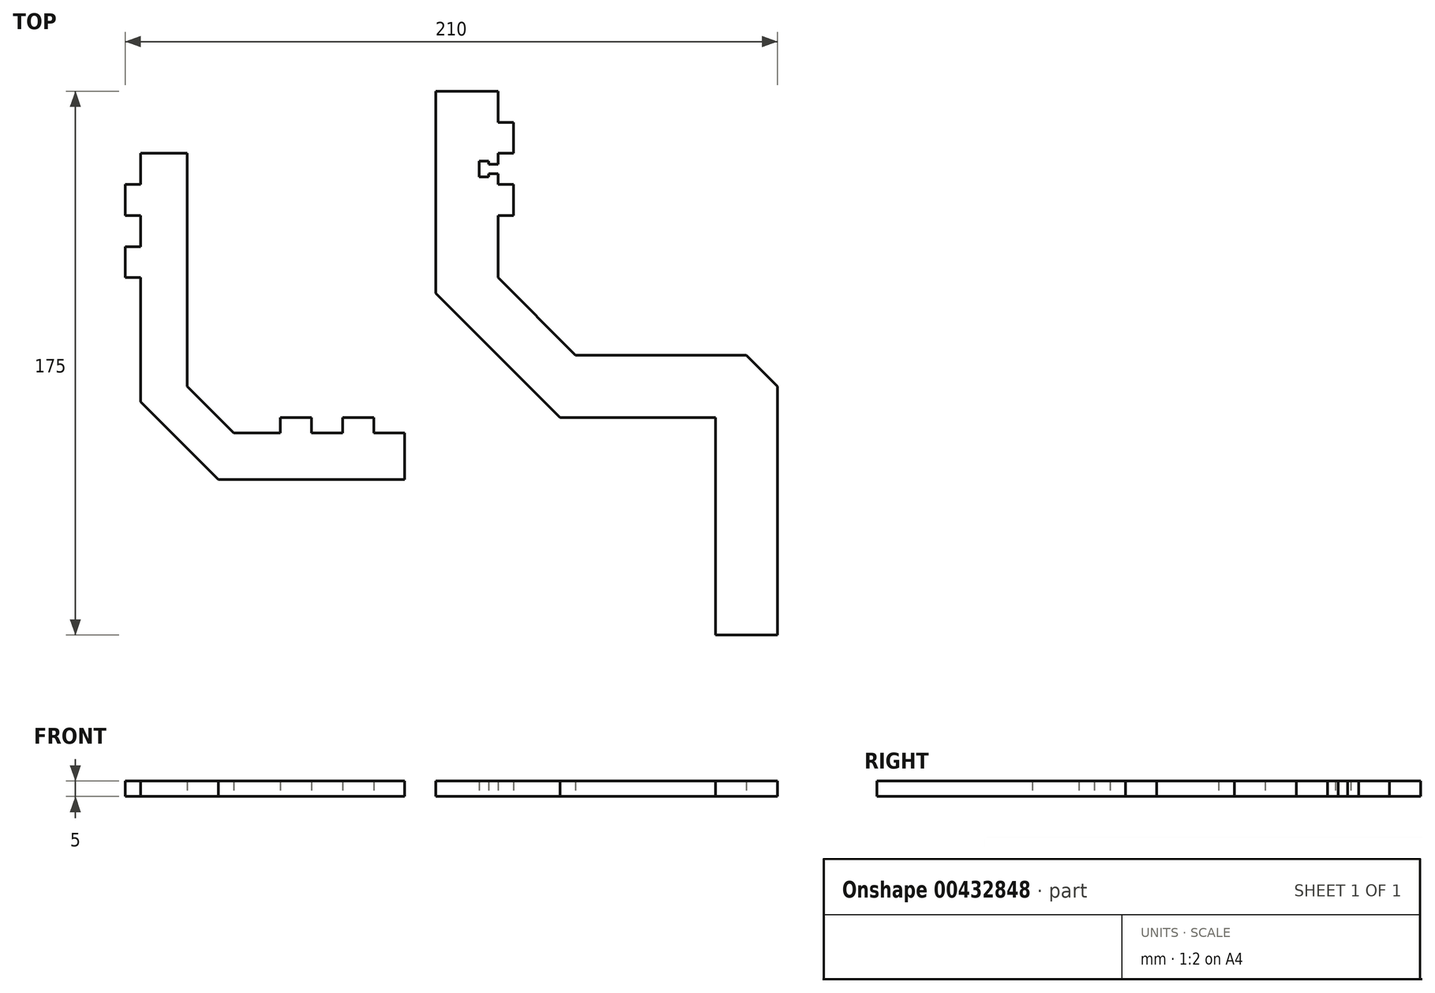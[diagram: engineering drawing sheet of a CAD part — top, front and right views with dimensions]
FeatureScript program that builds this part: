
annotation { "Feature Type Name" : "Feature", "Feature Type Description" : "" }
export const myFeature = defineFeature(function(context is Context, id is Id, definition is map)
    precondition{}
    {
        {
            var Q0;
            Q0=qCreatedBy(makeId("Top.planeOp"),FACE);
            var sketch = newSketch(context, id + "F0", { "sketchPlane" : qUnion([Q0])});
            skLineSegment(sketch, "E0.bottom", {"start": v(-20, 60) * mm, "end": v(0, 60) * mm});
            skLineSegment(sketch, "E0.left", {"start": v(-20, 60) * mm, "end": v(-20, -5) * mm});
            skLineSegment(sketch, "E0.right", {"start": v(0, 60) * mm, "end": v(0, 50) * mm});
            skLineSegment(sketch, "E1.bottom", {"start": v(25, -25) * mm, "end": v(80, -25) * mm});
            skLineSegment(sketch, "E1.top", {"start": v(20, -45) * mm, "end": v(70, -45) * mm});
            skLineSegment(sketch, "E2", {"start": v(0, 0) * mm, "end": v(25, -25) * mm});
            skLineSegment(sketch, "E3", {"start": v(-20, -5) * mm, "end": v(20, -45) * mm});
            skLineSegment(sketch, "E4.top", {"start": v(70, -115) * mm, "end": v(90, -115) * mm});
            skLineSegment(sketch, "E4.left", {"start": v(70, -45) * mm, "end": v(70, -115) * mm});
            skLineSegment(sketch, "E4.right", {"start": v(90, -35) * mm, "end": v(90, -115) * mm});
            skLineSegment(sketch, "E5", {"start": v(80, -25) * mm, "end": v(90, -35) * mm});
            skLineSegment(sketch, "E6", {"start": v(70, -45) * mm, "end": v(70, -45) * mm});
            skLineSegment(sketch, "E7.bottom", {"start": v(0, 50) * mm, "end": v(5, 50) * mm});
            skLineSegment(sketch, "E7.top", {"start": v(0, 40) * mm, "end": v(5, 40) * mm});
            skLineSegment(sketch, "E7.right", {"start": v(5, 50) * mm, "end": v(5, 40) * mm});
            skLineSegment(sketch, "E8.bottom", {"start": v(0, 30) * mm, "end": v(5, 30) * mm});
            skLineSegment(sketch, "E8.top", {"start": v(0, 20) * mm, "end": v(5, 20) * mm});
            skLineSegment(sketch, "E8.right", {"start": v(5, 30) * mm, "end": v(5, 20) * mm});
            skLineSegment(sketch, "E9.trimOffspring", {"start": v(0, 40) * mm, "end": v(0, 36.5) * mm});
            skLineSegment(sketch, "E10.trimOffspring", {"start": v(0, 20) * mm, "end": v(0, 0) * mm});
            skLineSegment(sketch, "E11.bottom", {"start": v(0, 36.5) * mm, "end": v(-3, 36.5) * mm});
            skLineSegment(sketch, "E11.top", {"start": v(0, 33.5) * mm, "end": v(-3, 33.5) * mm});
            skLineSegment(sketch, "E12.bottom", {"start": v(-6, 37.5) * mm, "end": v(-3, 37.5) * mm});
            skLineSegment(sketch, "E12.top", {"start": v(-6, 32.5) * mm, "end": v(-3, 32.5) * mm});
            skLineSegment(sketch, "E12.left", {"start": v(-6, 37.5) * mm, "end": v(-6, 32.5) * mm});
            skLineSegment(sketch, "E12.right", {"start": v(-3, 37.5) * mm, "end": v(-3, 36.5) * mm});
            skLineSegment(sketch, "E13.trimOffspring", {"start": v(-3, 33.5) * mm, "end": v(-3, 32.5) * mm});
            skLineSegment(sketch, "E14.trimOffspring", {"start": v(0, 33.5) * mm, "end": v(0, 30) * mm});
            skSolve(sketch);
        }
        {
            var Q0;
            Q0=makeQuery(id+"F0.imprint","IMPRINT",FACE,{"disambiguationData":[TD([[makeQuery(id+"F0.imprint","IMPRINT",EDGE,{"derivedFrom":sQuery(id+"F0.wireOp",EDGE,"E0.bottom")}),-1.0]])]});
            extrude(context, id + "F1", {"entities" : qUnion([Q0]), "depth" : 5 * mm});
        }
        {
            var Q0;
            Q0=qCreatedBy(makeId("Top.planeOp"),FACE);
            var sketch = newSketch(context, id + "F2", { "sketchPlane" : qUnion([Q0])});
            skLineSegment(sketch, "E15.bottom", {"start": v(-115, 40) * mm, "end": v(-100, 40) * mm});
            skLineSegment(sketch, "E15.left", {"start": v(-115, 40) * mm, "end": v(-115, 30) * mm});
            skLineSegment(sketch, "E15.right", {"start": v(-100, 40) * mm, "end": v(-100, -35) * mm});
            skLineSegment(sketch, "E16.top", {"start": v(-90, -65) * mm, "end": v(-30, -65) * mm});
            skLineSegment(sketch, "E16.right", {"start": v(-30, -50) * mm, "end": v(-30, -65) * mm});
            skLineSegment(sketch, "E17", {"start": v(-100, -35) * mm, "end": v(-85, -50) * mm});
            skLineSegment(sketch, "E18", {"start": v(-90, -65) * mm, "end": v(-115, -40) * mm});
            skLineSegment(sketch, "E19.bottom", {"start": v(-115, 30) * mm, "end": v(-120, 30) * mm});
            skLineSegment(sketch, "E19.top", {"start": v(-115, 20) * mm, "end": v(-120, 20) * mm});
            skLineSegment(sketch, "E19.right", {"start": v(-120, 30) * mm, "end": v(-120, 20) * mm});
            skLineSegment(sketch, "E20.bottom", {"start": v(-115, 10) * mm, "end": v(-120, 10) * mm});
            skLineSegment(sketch, "E20.top", {"start": v(-115, 0) * mm, "end": v(-120, 0) * mm});
            skLineSegment(sketch, "E20.right", {"start": v(-120, 10) * mm, "end": v(-120, 0) * mm});
            skLineSegment(sketch, "E21.top", {"start": v(-70, -45) * mm, "end": v(-60, -45) * mm});
            skLineSegment(sketch, "E21.left", {"start": v(-70, -50) * mm, "end": v(-70, -45) * mm});
            skLineSegment(sketch, "E21.right", {"start": v(-60, -50) * mm, "end": v(-60, -45) * mm});
            skLineSegment(sketch, "E22.top", {"start": v(-50, -45) * mm, "end": v(-40, -45) * mm});
            skLineSegment(sketch, "E22.left", {"start": v(-50, -50) * mm, "end": v(-50, -45) * mm});
            skLineSegment(sketch, "E22.right", {"start": v(-40, -50) * mm, "end": v(-40, -45) * mm});
            skLineSegment(sketch, "E23.trimOffspring", {"start": v(-115, 20) * mm, "end": v(-115, 10) * mm});
            skLineSegment(sketch, "E24.trimOffspring", {"start": v(-60, -50) * mm, "end": v(-50, -50) * mm});
            skLineSegment(sketch, "E25.trimOffspring", {"start": v(-40, -50) * mm, "end": v(-30, -50) * mm});
            skLineSegment(sketch, "E26", {"start": v(-85, -50) * mm, "end": v(-70, -50) * mm});
            skLineSegment(sketch, "E27.trimOffspring", {"start": v(-115, 0) * mm, "end": v(-115, -40) * mm});
            skSolve(sketch);
        }
        {
            var Q0;
            Q0=makeQuery(id+"F2.imprint","IMPRINT",FACE,{"disambiguationData":[TD([[makeQuery(id+"F2.imprint","IMPRINT",EDGE,{"derivedFrom":sQuery(id+"F2.wireOp",EDGE,"E15.bottom")}),-1.0]])]});
            extrude(context, id + "F3", {"entities" : qUnion([Q0]), "depth" : 5 * mm});
        }
    });
